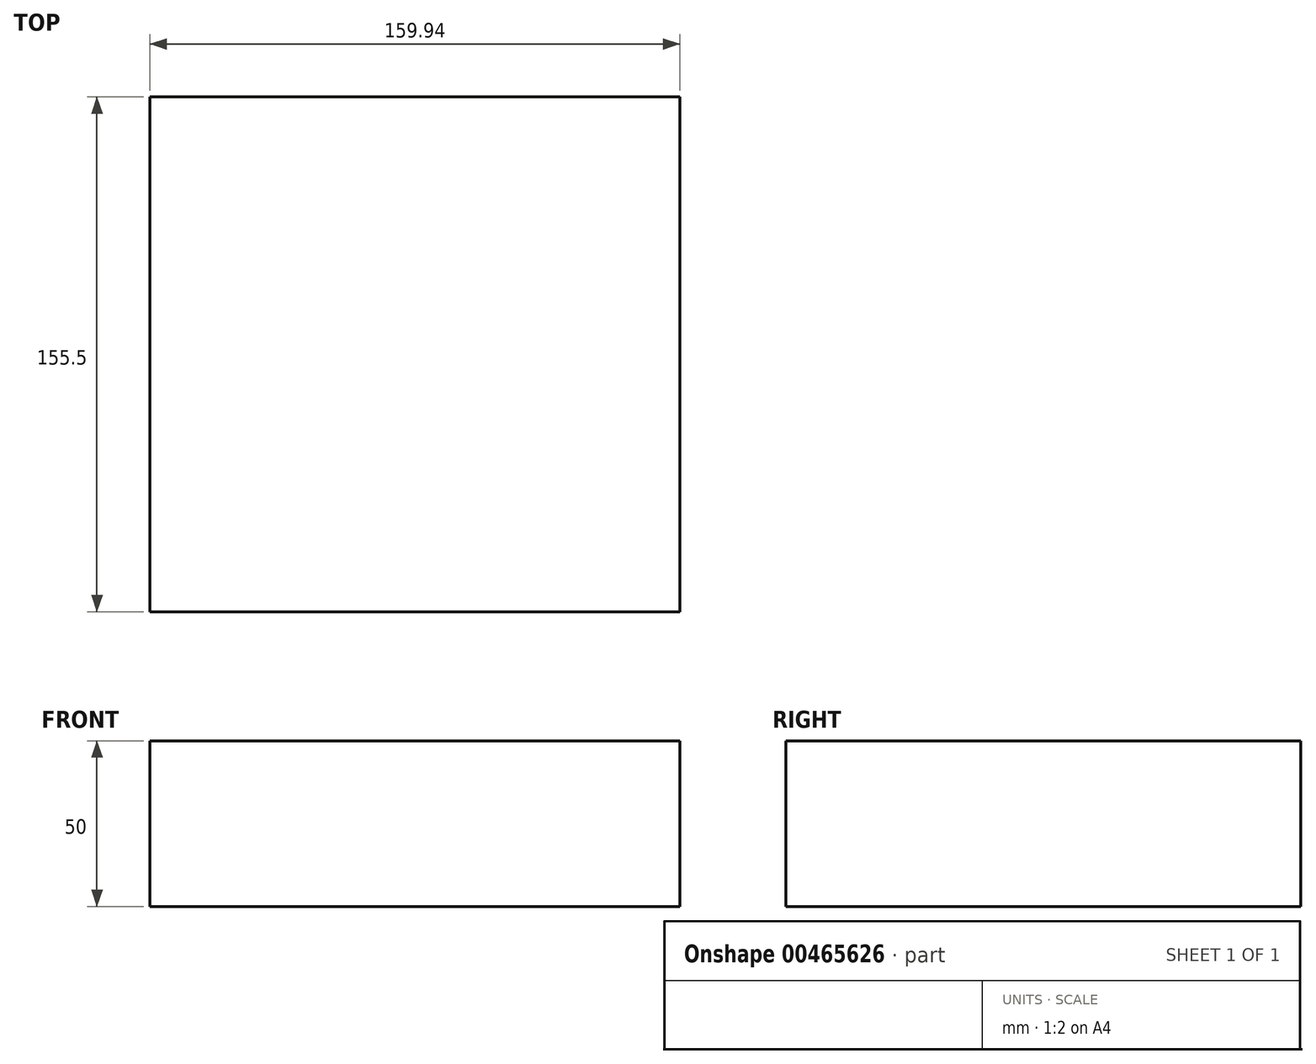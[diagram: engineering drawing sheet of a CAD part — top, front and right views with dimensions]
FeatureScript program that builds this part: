
annotation { "Feature Type Name" : "Feature", "Feature Type Description" : "" }
export const myFeature = defineFeature(function(context is Context, id is Id, definition is map)
    precondition{}
    {
        {
            var Q0;
            Q0=qCreatedBy(makeId("Top.planeOp"),FACE);
            var sketch = newSketch(context, id + "F0", { "sketchPlane" : qUnion([Q0])});
            skLineSegment(sketch, "E0.bottom", {"start": v(-93.75, 0) * mm, "end": v(66.19, 0) * mm});
            skLineSegment(sketch, "E0.top", {"start": v(-93.75, -155.5) * mm, "end": v(66.19, -155.5) * mm});
            skLineSegment(sketch, "E0.left", {"start": v(-93.75, 0) * mm, "end": v(-93.75, -155.5) * mm});
            skLineSegment(sketch, "E0.right", {"start": v(66.19, 0) * mm, "end": v(66.19, -155.5) * mm});
            skSolve(sketch);
        }
        {
            var Q0;
            Q0 = qSketchRegion(id + "F0", true);
            extrude(context, id + "F1", {"entities" : qUnion([Q0]), "depth" : 25 * mm});
        }
        {
            var Q0;
            Q0 = qSketchRegion(id + "F0", true);
            var Q1;
            Q1=makeQuery(id+"F1.opExtrude","CAP_FACE",FACE,{"disambiguationData":[OSD([sQuery(id+"F0.wireOp",EDGE,"E0.bottom"),sQuery(id+"F0.wireOp",EDGE,"E0.top"),sQuery(id+"F0.wireOp",EDGE,"E0.left"),sQuery(id+"F0.wireOp",EDGE,"E0.right")])],"isStart":false});
            extrude(context, id + "F2", {"entities" : qUnion([Q0, Q1]), "operationType" : NewBodyOperationType.ADD, "depth" : 25 * mm});
        }
    });
